# Revit family: P730011-030-30
name_source: partatom
category: Lighting Fixtures
revit_build: Autodesk Revit 2014 (Build: 20130308_1515(x64)
units: mm (PartAtom-declared; Revit-internal decimal feet)

## types (1)
- P730011-030-30
    Apparent Load = 20 VA
    Assembly Code = D5020200
    Color Filter = 16777215
    Connector Description = Lighting Connector
    Default Elevation = 48"
    Depth = 6 3/16"
    Description = The Wrap and Strip Collection’s Two-Foot LED Wrap Light features a crisp
white acrylic diffuser shaped into an elegant elongated tubular silhouette.
The light fixture is complemented by white end caps and a white metal chassis. The wrap light can be mounted on a wall or ceiling to meet your unique
design needs.
    Dimming Lamp Color Temperature Shift = <None>
    Emit Shape Visible in Rendering = No
    Emit from Rectangle Length = 23 3/4"
    Emit from Rectangle Width = 6 3/16"
    Features = White polycarbonate diffuser
• Features a crisp white acrylic diffuser shaped into an elongated tubular silhouette.
• Complemented by white end caps and a white metal chassis.
• Can be mounted on a wall or ceiling to meet your unique design needs.
• Ideal for kitchens, laundry rooms, garage utility areas, and work spaces.
• Damp location listed.
• Measures 23.724-inch width by 2.992-inch height.
• Uses one integrated LED bulb (20w).
• Able to be fully dimmable with dimmable bulbs.
• Includes installation instructions and mounting hardware.
• Progress Lighting products are designed for exceptional quality, reliability, and functionality.
• Dimmable to 10% brightness (See Dimming Notes)
• Mounting backplate for outlet box included
• 6 in of wire supplied
    Fixture distribution = Direct
    Glass = Hubbell - Glass
    Height = 2 15/16"
    Housing Material = Paint - Hubbell - White Texture
    Lamp = LED
    Length = 23 3/4"
    Load Classification = Lighting
    Manufacturer = Progress Lighting
    Model = P730011-030-30
    Mounting = Paint - Hubbell - Light Silver
    Photometric Web File = generic.ies
    Power Factor = 1
    Product Documentation Link = https://hubbellcdn.com
    Product Link = https://www.hubbell.com
    Reflector Finish = Hubbell - White Glass
    Tilt Angle = -90.00°
    URL = https://www.hubbell.com
    Voltage = 120 V
    Warranty = 5 years Warranty
    Wattage Comments = 20W
    Watts = 20 W
    Wings = Paint - Hubbell - Light Silver

## geometry (parser evidence)
native form markers: Sweep x4
no freeform markers — native parametric forms only
